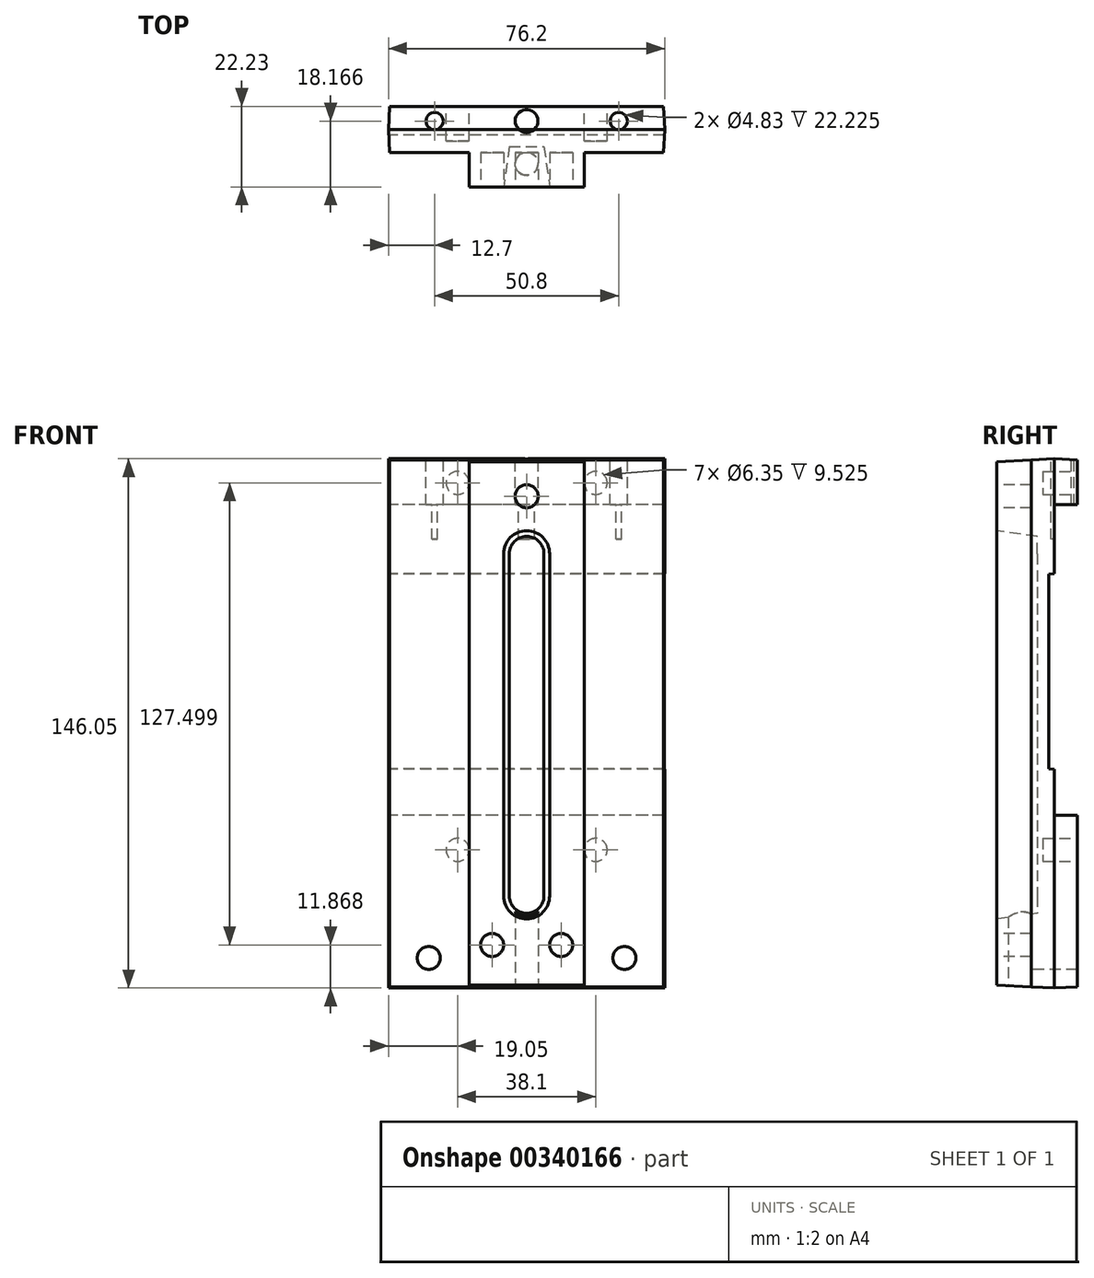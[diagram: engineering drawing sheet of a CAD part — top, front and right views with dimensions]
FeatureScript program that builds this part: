
annotation { "Feature Type Name" : "Feature", "Feature Type Description" : "" }
export const myFeature = defineFeature(function(context is Context, id is Id, definition is map)
    precondition{}
    {
        {
            var Q0;
            Q0=qCreatedBy(makeId("Front.planeOp"),FACE);
            var sketch = newSketch(context, id + "F0", { "sketchPlane" : qUnion([Q0])});
            skLineSegment(sketch, "E0.bottom", {"start": v(0, 0) * mm, "end": v(76.2, 0) * mm});
            skLineSegment(sketch, "E0.top", {"start": v(0, 146.05) * mm, "end": v(76.2, 146.05) * mm});
            skLineSegment(sketch, "E0.left", {"start": v(0, 0) * mm, "end": v(0, 146.05) * mm});
            skLineSegment(sketch, "E0.right", {"start": v(76.2, 0) * mm, "end": v(76.2, 146.05) * mm});
            skSolve(sketch);
        }
        {
            var Q0;
            Q0 = qSketchRegion(id + "F0", true);
            extrude(context, id + "F1", {"entities" : qUnion([Q0]), "depth" : 15.88 * mm, "hasDraft" : true, "draftAngle" : 3 * degree, "draftPullDirection" : true, "hasSecondDirection" : true, "secondDirectionOppositeDirection" : true, "secondDirectionDepth" : 6.35 * mm, "hasSecondDirectionDraft" : true, "secondDirectionDraftAngle" : 3 * degree, "secondDirectionDraftPullDirection" : true});
        }
        {
            var Q0;
            Q0=qCreatedBy(makeId("Top.planeOp"),FACE);
            var sketch = newSketch(context, id + "F2", { "sketchPlane" : qUnion([Q0])});
            skLineSegment(sketch, "E1.0.0", {"start": v(0.83, -15.87) * mm, "end": v(0, 0) * mm});
            skLineSegment(sketch, "E1.0.1", {"start": v(0, 0) * mm, "end": v(76.2, 0) * mm});
            skLineSegment(sketch, "E1.0.2", {"start": v(76.2, 0) * mm, "end": v(75.37, -15.87) * mm});
            skLineSegment(sketch, "E1.0.3", {"start": v(0.83, -15.88) * mm, "end": v(75.37, -15.88) * mm});
            skLineSegment(sketch, "E2.bottom", {"start": v(22.22, -6.35) * mm, "end": v(-20.56, -6.35) * mm});
            skLineSegment(sketch, "E2.top", {"start": v(22.22, -25.4) * mm, "end": v(-20.56, -25.4) * mm});
            skLineSegment(sketch, "E2.left", {"start": v(22.22, -6.35) * mm, "end": v(22.22, -25.4) * mm});
            skLineSegment(sketch, "E2.right", {"start": v(-20.56, -6.35) * mm, "end": v(-20.56, -25.4) * mm});
            skPoint(sketch, "E2.middle", {"position": v(0.83, -15.87) * mm});
            skLineSegment(sketch, "E3.bottom", {"start": v(53.98, -6.35) * mm, "end": v(96.76, -6.35) * mm});
            skLineSegment(sketch, "E3.top", {"start": v(53.98, -25.4) * mm, "end": v(96.76, -25.4) * mm});
            skLineSegment(sketch, "E3.left", {"start": v(53.98, -6.35) * mm, "end": v(53.98, -25.4) * mm});
            skLineSegment(sketch, "E3.right", {"start": v(96.76, -6.35) * mm, "end": v(96.76, -25.4) * mm});
            skPoint(sketch, "E3.middle", {"position": v(75.37, -15.87) * mm});
            skSolve(sketch);
        }
        {
            var Q0;
            {var subQ0=sQuery(id+"F2.wireOp",EDGE,"E1.0.3");var subQ1=sQuery(id+"F2.wireOp",EDGE,"E1.0.0");var subQ2=makeQuery(id+"F2.imprint","INTERSECT",VERTEX,{"derivedFrom":[subQ1,subQ0]});Q0=makeQuery(id+"F2.imprint","IMPRINT",FACE,{"disambiguationData":[TD([[makeQuery(id+"F2.imprint","IMPRINT",EDGE,{"disambiguationData":[TD([[subQ2,-1.0]])],"derivedFrom":subQ1}),-1.0]])]});}
            var Q1;
            {var subQ0=sQuery(id+"F2.wireOp",EDGE,"E1.0.3");var subQ1=sQuery(id+"F2.wireOp",EDGE,"E1.0.2");var subQ2=makeQuery(id+"F2.imprint","INTERSECT",VERTEX,{"derivedFrom":[subQ1,subQ0]});Q1=makeQuery(id+"F2.imprint","IMPRINT",FACE,{"disambiguationData":[TD([[makeQuery(id+"F2.imprint","IMPRINT",EDGE,{"disambiguationData":[TD([[subQ2,1.0]])],"derivedFrom":subQ1}),-1.0]])]});}
            extrude(context, id + "F3", {"entities" : qUnion([Q0, Q1]), "operationType" : NewBodyOperationType.REMOVE, "endBound" : BoundingType.THROUGH_ALL, "depth" : 25.4 * mm});
        }
        {
            var Q0;
            Q0=qCreatedBy(makeId("Right.planeOp"),FACE);
            var sketch = newSketch(context, id + "F4", { "sketchPlane" : qUnion([Q0])});
            skLineSegment(sketch, "E4.0", {"start": v(6.35, 0.33) * mm, "end": v(6.35, 145.72) * mm});
            skLineSegment(sketch, "E5.0.0", {"start": v(-6.35, 145.72) * mm, "end": v(0, 146.05) * mm});
            skLineSegment(sketch, "E5.0.1", {"start": v(-6.35, 145.72) * mm, "end": v(-6.35, 0.33) * mm});
            skLineSegment(sketch, "E5.0.2", {"start": v(-6.35, 0.33) * mm, "end": v(0, 0) * mm});
            skLineSegment(sketch, "E5.0.3", {"start": v(0, 0) * mm, "end": v(0, 146.05) * mm});
            skLineSegment(sketch, "E6", {"start": v(6.35, 133.35) * mm, "end": v(0, 133.35) * mm});
            skLineSegment(sketch, "E7", {"start": v(0, 133.35) * mm, "end": v(0, 114.3) * mm});
            skLineSegment(sketch, "E8", {"start": v(0, 114.3) * mm, "end": v(-1.59, 114.22) * mm});
            skLineSegment(sketch, "E9", {"start": v(-1.59, 114.22) * mm, "end": v(-1.59, 60.4) * mm});
            skLineSegment(sketch, "E10", {"start": v(-1.59, 60.4) * mm, "end": v(0, 60.33) * mm});
            skLineSegment(sketch, "E11", {"start": v(0, 60.33) * mm, "end": v(0, 47.63) * mm});
            skLineSegment(sketch, "E12", {"start": v(0, 47.63) * mm, "end": v(6.35, 47.63) * mm});
            skSolve(sketch);
        }
        {
            var Q0;
            {var subQ1=sQuery(id+"F4.wireOp",EDGE,"E6");Q0=makeQuery(id+"F4.imprint","IMPRINT",FACE,{"disambiguationData":[TD([[makeQuery(id+"F4.imprint","IMPRINT",EDGE,{"derivedFrom":subQ1}),1.0]])]});}
            var Q1;
            {var subQ0=sQuery(id+"F4.wireOp",EDGE,"E8");Q1=makeQuery(id+"F4.imprint","IMPRINT",FACE,{"disambiguationData":[TD([[makeQuery(id+"F4.imprint","IMPRINT",EDGE,{"derivedFrom":subQ0}),1.0]])]});}
            extrude(context, id + "F5", {"entities" : qUnion([Q0, Q1]), "operationType" : NewBodyOperationType.REMOVE, "endBound" : BoundingType.THROUGH_ALL, "depth" : 25.4 * mm});
        }
        {
            var Q0;
            Q0=makeQuery(id+"F1.opExtrude","CAP_FACE",FACE,{"disambiguationData":[OSD([sQuery(id+"F0.wireOp",EDGE,"E0.bottom"),sQuery(id+"F0.wireOp",EDGE,"E0.top"),sQuery(id+"F0.wireOp",EDGE,"E0.left"),sQuery(id+"F0.wireOp",EDGE,"E0.right")])],"isStart":false});
            var sketch = newSketch(context, id + "F6", { "sketchPlane" : qUnion([Q0])});
            skLineSegment(sketch, "E13", {"start": v(38.1, 145.22) * mm, "end": v(38.1, 0) * mm, "construction": true});
            skLineSegment(sketch, "E14.bottom", {"start": v(44.45, 25.4) * mm, "end": v(31.75, 25.4) * mm});
            skLineSegment(sketch, "E14.top", {"start": v(44.45, 119.82) * mm, "end": v(31.75, 119.82) * mm});
            skLineSegment(sketch, "E14.left", {"start": v(44.45, 25.4) * mm, "end": v(44.45, 119.82) * mm});
            skLineSegment(sketch, "E14.right", {"start": v(31.75, 25.4) * mm, "end": v(31.75, 119.82) * mm});
            skPoint(sketch, "E14.middle", {"position": v(38.1, 72.6) * mm});
            skCircle(sketch, "E15", {"center": v(38.1, 119.82) * mm, "radius": 6.35 * mm});
            skCircle(sketch, "E16", {"center": v(38.1, 25.4) * mm, "radius": 6.35 * mm});
            skSolve(sketch);
        }
        {
            var Q0;
            Q0 = qSketchRegion(id + "F6", true);
            extrude(context, id + "F7", {"entities" : qUnion([Q0]), "operationType" : NewBodyOperationType.REMOVE, "oppositeDirection" : true, "depth" : 11.1 * mm, "hasDraft" : true, "draftAngle" : 8 * degree, "draftPullDirection" : true});
        }
        {
            var Q0;
            Q0=makeQuery(id+"F1.opExtrude","CAP_FACE",FACE,{"disambiguationData":[OSD([sQuery(id+"F0.wireOp",EDGE,"E0.bottom"),sQuery(id+"F0.wireOp",EDGE,"E0.top"),sQuery(id+"F0.wireOp",EDGE,"E0.left"),sQuery(id+"F0.wireOp",EDGE,"E0.right")])],"isStart":false});
            var sketch = newSketch(context, id + "F8", { "sketchPlane" : qUnion([Q0])});
            skLineSegment(sketch, "E17", {"start": v(38.1, 145.22) * mm, "end": v(38.1, 0) * mm});
            skLineSegment(sketch, "E18", {"start": v(28.58, 11.87) * mm, "end": v(47.63, 11.87) * mm});
            skPoint(sketch, "E19", {"position": v(38.1, 11.87) * mm});
            skCircle(sketch, "E20", {"center": v(28.58, 11.87) * mm, "radius": 3.18 * mm});
            skCircle(sketch, "E21", {"center": v(47.63, 11.87) * mm, "radius": 3.18 * mm});
            skCircle(sketch, "E22", {"center": v(38.1, 135.7) * mm, "radius": 3.18 * mm});
            skSolve(sketch);
        }
        {
            var Q0;
            Q0 = qSketchRegion(id + "F8", true);
            extrude(context, id + "F9", {"entities" : qUnion([Q0]), "operationType" : NewBodyOperationType.REMOVE, "oppositeDirection" : true, "depth" : 9.52 * mm});
        }
        {
            var Q0;
            {var subQ0=sQuery(id+"F0.wireOp",EDGE,"E0.top");var subQ1=sQuery(id+"F0.wireOp",EDGE,"E0.left");var subQ2=sQuery(id+"F0.wireOp",EDGE,"E0.right");Q0=makeQuery(id+"F5.boolean.opBoolean","SPLIT",FACE,{"disambiguationData":[TD([makeQuery(id+"F1.opExtrude","SWEPT_FACE",FACE,{"disambiguationData":[OSD([subQ0])]})])],"derivedFrom":makeQuery(id+"F1.opExtrude","CAP_FACE",FACE,{"disambiguationData":[OSD([sQuery(id+"F0.wireOp",EDGE,"E0.bottom"),subQ0,subQ1,subQ2])],"isStart":true})});}
            var sketch = newSketch(context, id + "F10", { "sketchPlane" : qUnion([Q0])});
            skLineSegment(sketch, "E23", {"start": v(-38.1, 145.72) * mm, "end": v(-38.1, 0) * mm});
            skLineSegment(sketch, "E24", {"start": v(-57.15, 139.37) * mm, "end": v(-19.05, 139.37) * mm});
            skLineSegment(sketch, "E25", {"start": v(-57.15, 38.1) * mm, "end": v(-19.05, 38.1) * mm});
            skPoint(sketch, "E26", {"position": v(-38.1, 139.37) * mm});
            skPoint(sketch, "E27", {"position": v(-38.1, 38.1) * mm});
            skCircle(sketch, "E28", {"center": v(-19.05, 139.37) * mm, "radius": 3.18 * mm});
            skCircle(sketch, "E29", {"center": v(-57.15, 139.37) * mm, "radius": 3.18 * mm});
            skCircle(sketch, "E30", {"center": v(-19.05, 38.1) * mm, "radius": 3.18 * mm});
            skCircle(sketch, "E31", {"center": v(-57.15, 38.1) * mm, "radius": 3.18 * mm});
            skSolve(sketch);
        }
        {
            var Q0;
            Q0 = qSketchRegion(id + "F10", true);
            extrude(context, id + "F11", {"entities" : qUnion([Q0]), "operationType" : NewBodyOperationType.REMOVE, "oppositeDirection" : true, "depth" : 9.52 * mm});
        }
        {
            var Q0;
            {var subQ0=makeQuery(id+"F1.opExtrude","SWEPT_FACE",FACE,{"disambiguationData":[OSD([sQuery(id+"F0.wireOp",EDGE,"E0.right")])]});var subQ1=makeQuery(id+"F1.opExtrude","SWEPT_FACE",FACE,{"disambiguationData":[OSD([sQuery(id+"F0.wireOp",EDGE,"E0.top")])]});Q0=makeQuery(id+"F1.*.booleanUnion.opBoolean","MERGE",VERTEX,{"derivedFrom":[makeQuery(id+"F1.*.split.splitOp","SPLIT_SURFACE_INTERSECT",VERTEX,{"derivedFrom":[subQ1,subQ0]}),makeQuery(id+"F1.*.split.splitOp","SPLIT_SURFACE_INTERSECT",VERTEX,{"derivedFrom":[subQ1,subQ0],"isFromBackBody":true})]});}
            var Q1;
            Q1=qCreatedBy(makeId("Top.planeOp"),FACE);
            cPlane(context, id + "F12", {"entities" : qUnion([Q0, Q1]), "cplaneType" : CPlaneType.PLANE_POINT, "offset" : 25.4 * mm, "width" : 152.4 * mm, "height" : 152.4 * mm});
        }
        {
            var Q0;
            Q0=qCreatedBy(id+"F12.planeOp",FACE);
            var sketch = newSketch(context, id + "F13", { "sketchPlane" : qUnion([Q0])});
            skCircle(sketch, "E32", {"center": v(12.7, 2.29) * mm, "radius": 2.41 * mm});
            skCircle(sketch, "E33", {"center": v(63.5, 2.29) * mm, "radius": 2.41 * mm});
            skLineSegment(sketch, "E34.0.0", {"start": v(0.33, 6.35) * mm, "end": v(0, 0) * mm});
            skLineSegment(sketch, "E34.0.1", {"start": v(0, 0) * mm, "end": v(76.2, 0) * mm});
            skLineSegment(sketch, "E34.0.2", {"start": v(76.2, 0) * mm, "end": v(75.87, 6.35) * mm});
            skLineSegment(sketch, "E34.0.3", {"start": v(75.87, 6.35) * mm, "end": v(0.33, 6.35) * mm, "construction": true});
            skCircle(sketch, "E35", {"center": v(38.1, 2.29) * mm, "radius": 3.18 * mm});
            skLineSegment(sketch, "E36", {"start": v(38.1, 6.35) * mm, "end": v(38.1, 2.29) * mm, "construction": true});
            skSolve(sketch);
        }
        {
            var Q0;
            Q0 = qSketchRegion(id + "F13", true);
            extrude(context, id + "F14", {"entities" : qUnion([Q0]), "operationType" : NewBodyOperationType.REMOVE, "oppositeDirection" : true, "depth" : 22.22 * mm});
        }
        {
            var Q0;
            Q0=qCreatedBy(makeId("Top.planeOp"),FACE);
            var sketch = newSketch(context, id + "F15", { "sketchPlane" : qUnion([Q0])});
            skCircle(sketch, "E37", {"center": v(38.1, -9.52) * mm, "radius": 3.18 * mm});
            skSolve(sketch);
        }
        {
            var Q0;
            Q0 = qSketchRegion(id + "F15", true);
            extrude(context, id + "F16", {"entities" : qUnion([Q0]), "operationType" : NewBodyOperationType.REMOVE, "depth" : 25.4 * mm});
        }
        {
            var Q0;
            Q0=makeQuery(id+"F3.boolean.opBoolean","COPY",FACE,{"derivedFrom":makeQuery(id+"F3.opExtrude","SWEPT_FACE",FACE,{"disambiguationData":[OSD([sQuery(id+"F2.wireOp",EDGE,"E3.bottom")])]})});
            var sketch = newSketch(context, id + "F17", { "sketchPlane" : qUnion([Q0])});
            skLineSegment(sketch, "E38.0", {"start": v(22.22, 145.72) * mm, "end": v(22.22, 0.33) * mm});
            skLineSegment(sketch, "E39.0", {"start": v(0, 0) * mm, "end": v(0, 47.62) * mm});
            skLineSegment(sketch, "E40.0", {"start": v(53.98, 145.72) * mm, "end": v(53.98, 0.33) * mm});
            skLineSegment(sketch, "E41.0", {"start": v(76.2, 0) * mm, "end": v(76.2, 47.62) * mm});
            skLineSegment(sketch, "E42", {"start": v(53.98, 8.27) * mm, "end": v(76.2, 8.27) * mm});
            skLineSegment(sketch, "E43", {"start": v(0, 8.27) * mm, "end": v(22.22, 8.27) * mm});
            skCircle(sketch, "E44", {"center": v(11.11, 8.27) * mm, "radius": 3.18 * mm});
            skCircle(sketch, "E45", {"center": v(65.09, 8.27) * mm, "radius": 3.18 * mm});
            skSolve(sketch);
        }
        {
            var Q0;
            Q0 = qSketchRegion(id + "F17", true);
            extrude(context, id + "F18", {"entities" : qUnion([Q0]), "operationType" : NewBodyOperationType.REMOVE, "endBound" : BoundingType.THROUGH_ALL, "oppositeDirection" : true, "depth" : 25.4 * mm});
        }
    });
